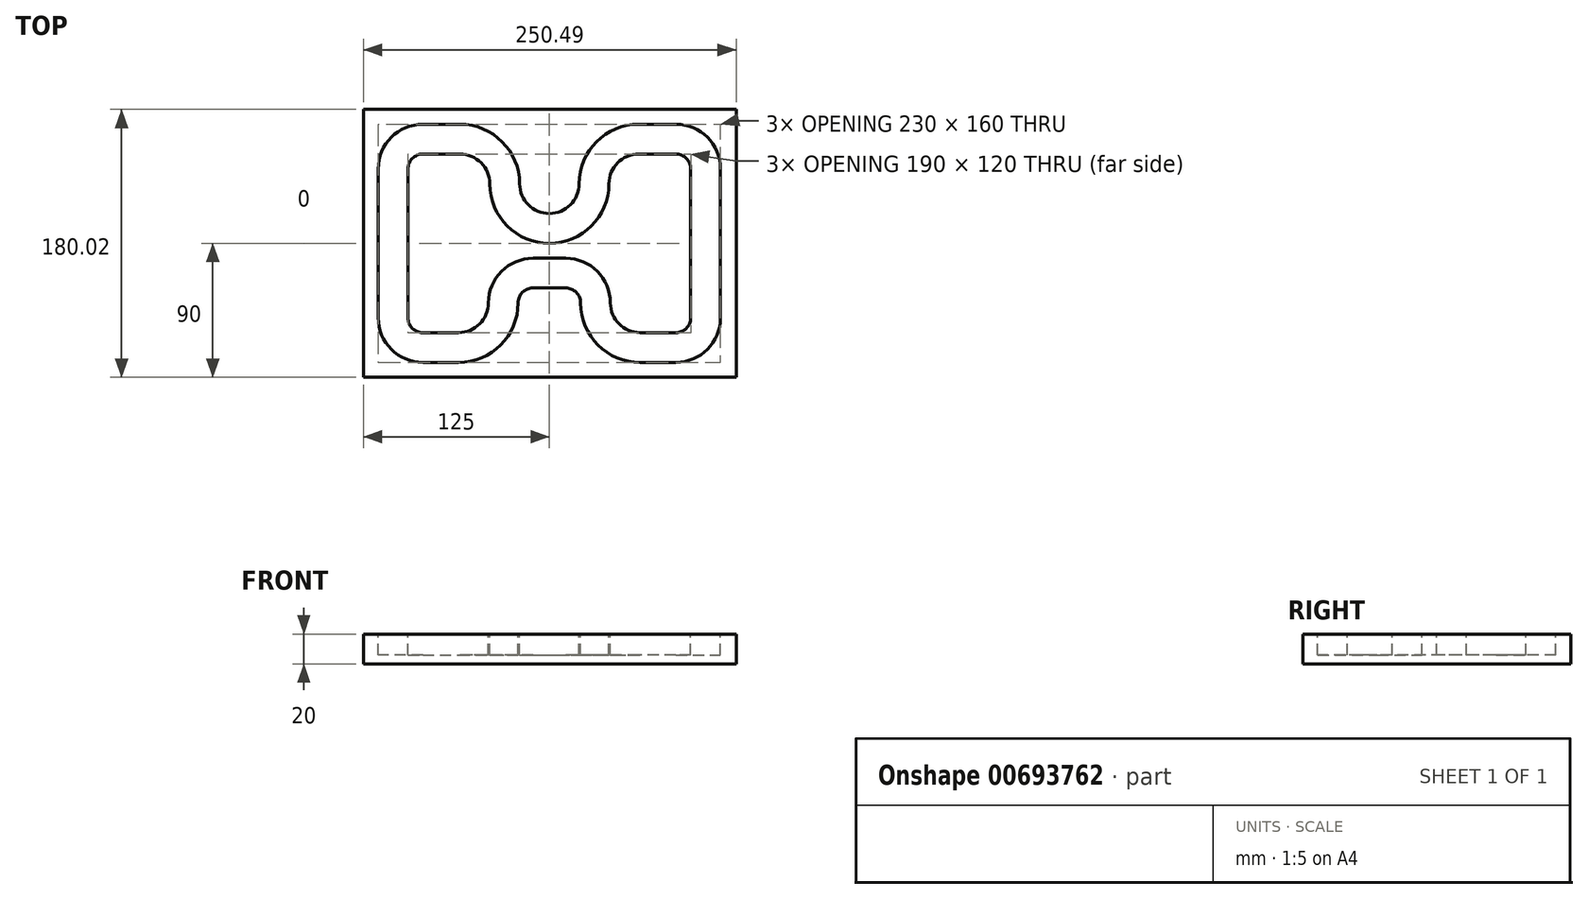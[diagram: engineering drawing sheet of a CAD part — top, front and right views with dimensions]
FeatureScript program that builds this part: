
annotation { "Feature Type Name" : "Feature", "Feature Type Description" : "" }
export const myFeature = defineFeature(function(context is Context, id is Id, definition is map)
    precondition{}
    {
        {
            var Q0;
            Q0=qCreatedBy(makeId("Top.planeOp"),FACE);
            var sketch = newSketch(context, id + "F0", { "sketchPlane" : qUnion([Q0])});
            skLineSegment(sketch, "E0.bottom", {"start": v(0, 0) * mm, "end": v(250, 0) * mm});
            skLineSegment(sketch, "E0.top", {"start": v(0, 180) * mm, "end": v(250, 180) * mm});
            skLineSegment(sketch, "E0.left", {"start": v(0, 0) * mm, "end": v(0, 180) * mm});
            skLineSegment(sketch, "E0.right", {"start": v(250, 0) * mm, "end": v(250, 180) * mm});
            skLineSegment(sketch, "E1.bottom", {"start": v(40, 170) * mm, "end": v(65, 170) * mm});
            skLineSegment(sketch, "E1.top", {"start": v(40, 10) * mm, "end": v(64, 10) * mm});
            skLineSegment(sketch, "E1.left", {"start": v(10, 140) * mm, "end": v(10, 40) * mm});
            skArc(sketch, "E2.filletArc", {"start": v(40, 170) * mm, "mid": v(18.79, 161.21) * mm, "end": v(10, 140) * mm});
            skArc(sketch, "E3.filletArc", {"start": v(10, 40) * mm, "mid": v(18.79, 18.79) * mm, "end": v(40, 10) * mm});
            skArc(sketch, "E4.filletArc", {"start": v(105, 130) * mm, "mid": v(93.28, 158.28) * mm, "end": v(65, 170) * mm});
            skArc(sketch, "E5", {"start": v(105, 130) * mm, "mid": v(110.86, 115.86) * mm, "end": v(125, 110) * mm});
            skPoint(sketch, "E6.orphan", {"position": v(125, 180) * mm});
            skPoint(sketch, "E7.end.orphan", {"position": v(125, 0) * mm});
            skPoint(sketch, "E8.end.orphan", {"position": v(104, 50) * mm});
            skArc(sketch, "E9", {"start": v(64, 10) * mm, "mid": v(92.28, 21.72) * mm, "end": v(104, 50) * mm});
            skArc(sketch, "E10.0", {"start": v(64, 30) * mm, "mid": v(78.14, 35.86) * mm, "end": v(84, 50) * mm});
            skLineSegment(sketch, "E10.1", {"start": v(40, 30) * mm, "end": v(64, 30) * mm});
            skArc(sketch, "E10.2", {"start": v(30, 40) * mm, "mid": v(32.93, 32.93) * mm, "end": v(40, 30) * mm});
            skArc(sketch, "E10.3", {"start": v(85, 130) * mm, "mid": v(79.14, 144.14) * mm, "end": v(65, 150) * mm});
            skLineSegment(sketch, "E10.4", {"start": v(40, 150) * mm, "end": v(65, 150) * mm});
            skArc(sketch, "E10.5", {"start": v(40, 150) * mm, "mid": v(32.93, 147.07) * mm, "end": v(30, 140) * mm});
            skLineSegment(sketch, "E10.6", {"start": v(30, 140) * mm, "end": v(30, 40) * mm});
            skLineSegment(sketch, "E11", {"start": v(125, 0) * mm, "end": v(125, 180) * mm, "construction": true});
            skArc(sketch, "E12", {"start": v(85, 130) * mm, "mid": v(96.72, 101.72) * mm, "end": v(125, 90) * mm});
            skArc(sketch, "E13", {"start": v(104, 50) * mm, "mid": v(106.93, 57.07) * mm, "end": v(114, 60) * mm});
            skLineSegment(sketch, "E14", {"start": v(114, 60) * mm, "end": v(125, 60) * mm});
            skLineSegment(sketch, "E15.0", {"start": v(114, 80) * mm, "end": v(125, 80) * mm});
            skArc(sketch, "E15.1", {"start": v(84, 50) * mm, "mid": v(92.79, 71.21) * mm, "end": v(114, 80) * mm});
            skArc(sketch, "E16.MirrorCS", {"start": v(145, 130) * mm, "mid": v(139.14, 115.86) * mm, "end": v(125, 110) * mm});
            skArc(sketch, "E17.MirrorCS", {"start": v(145, 130) * mm, "mid": v(156.72, 158.28) * mm, "end": v(185, 170) * mm});
            skLineSegment(sketch, "E18.MirrorCS", {"start": v(210, 170) * mm, "end": v(185, 170) * mm});
            skArc(sketch, "E19.MirrorCS", {"start": v(210, 170) * mm, "mid": v(231.21, 161.21) * mm, "end": v(240, 140) * mm});
            skLineSegment(sketch, "E20.MirrorCS", {"start": v(240, 140) * mm, "end": v(240, 40) * mm});
            skArc(sketch, "E21.MirrorCS", {"start": v(240, 40) * mm, "mid": v(231.21, 18.79) * mm, "end": v(210, 10) * mm});
            skLineSegment(sketch, "E22.MirrorCS", {"start": v(210, 10) * mm, "end": v(186, 10) * mm});
            skArc(sketch, "E23.MirrorCS", {"start": v(186, 10) * mm, "mid": v(157.72, 21.72) * mm, "end": v(146, 50) * mm});
            skArc(sketch, "E24.MirrorCS", {"start": v(146, 50) * mm, "mid": v(143.07, 57.07) * mm, "end": v(136, 60) * mm});
            skLineSegment(sketch, "E25.MirrorCS", {"start": v(136, 60) * mm, "end": v(125, 60) * mm});
            skLineSegment(sketch, "E26.MirrorCS", {"start": v(136, 80) * mm, "end": v(125, 80) * mm});
            skArc(sketch, "E27.MirrorCS", {"start": v(166, 50) * mm, "mid": v(157.21, 71.21) * mm, "end": v(136, 80) * mm});
            skArc(sketch, "E28.MirrorCS", {"start": v(186, 30) * mm, "mid": v(171.86, 35.86) * mm, "end": v(166, 50) * mm});
            skLineSegment(sketch, "E29.MirrorCS", {"start": v(210, 30) * mm, "end": v(186, 30) * mm});
            skArc(sketch, "E30.MirrorCS", {"start": v(220, 40) * mm, "mid": v(217.07, 32.93) * mm, "end": v(210, 30) * mm});
            skLineSegment(sketch, "E31.MirrorCS", {"start": v(220, 140) * mm, "end": v(220, 40) * mm});
            skArc(sketch, "E32.MirrorCS", {"start": v(210, 150) * mm, "mid": v(217.07, 147.07) * mm, "end": v(220, 140) * mm});
            skLineSegment(sketch, "E33.MirrorCS", {"start": v(210, 150) * mm, "end": v(185, 150) * mm});
            skArc(sketch, "E34.MirrorCS", {"start": v(165, 130) * mm, "mid": v(170.86, 144.14) * mm, "end": v(185, 150) * mm});
            skArc(sketch, "E35.MirrorCS", {"start": v(165, 130) * mm, "mid": v(153.28, 101.72) * mm, "end": v(125, 90) * mm});
            skSolve(sketch);
        }
        {
            var Q0;
            Q0=qCreatedBy(makeId("Top.planeOp"),FACE);
            cPlane(context, id + "F1", {"entities" : qUnion([Q0]), "cplaneType" : CPlaneType.OFFSET, "offset" : 20 * mm, "oppositeDirection" : true, "width" : 150 * mm, "height" : 150 * mm});
        }
        {
            var Q0;
            Q0=qCreatedBy(id+"F1.planeOp",FACE);
            var sketch = newSketch(context, id + "F2", { "sketchPlane" : qUnion([Q0])});
            skLineSegment(sketch, "E36.bottom", {"start": v(0, 0) * mm, "end": v(250.49, 0) * mm});
            skLineSegment(sketch, "E36.top", {"start": v(0, 180.02) * mm, "end": v(250.49, 180.02) * mm});
            skLineSegment(sketch, "E36.left", {"start": v(0, 0) * mm, "end": v(0, 180.02) * mm});
            skLineSegment(sketch, "E36.right", {"start": v(250.49, 0) * mm, "end": v(250.49, 180.02) * mm});
            skSolve(sketch);
        }
        {
            var Q0;
            Q0 = qSketchRegion(id + "F2", true);
            extrude(context, id + "F3", {"entities" : qUnion([Q0]), "depth" : 20 * mm, "offsetDistance" : 25 * mm});
        }
        {
            var Q0;
            Q0=makeQuery(id+"F0.imprint","IMPRINT",FACE,{"disambiguationData":[TD([[makeQuery(id+"F0.imprint","IMPRINT",EDGE,{"derivedFrom":sQuery(id+"F0.wireOp",EDGE,"E1.top")}),1.0]])]});
            extrude(context, id + "F4", {"entities" : qUnion([Q0]), "operationType" : NewBodyOperationType.REMOVE, "oppositeDirection" : true, "depth" : 14 * mm, "offsetDistance" : 25 * mm});
        }
    });
